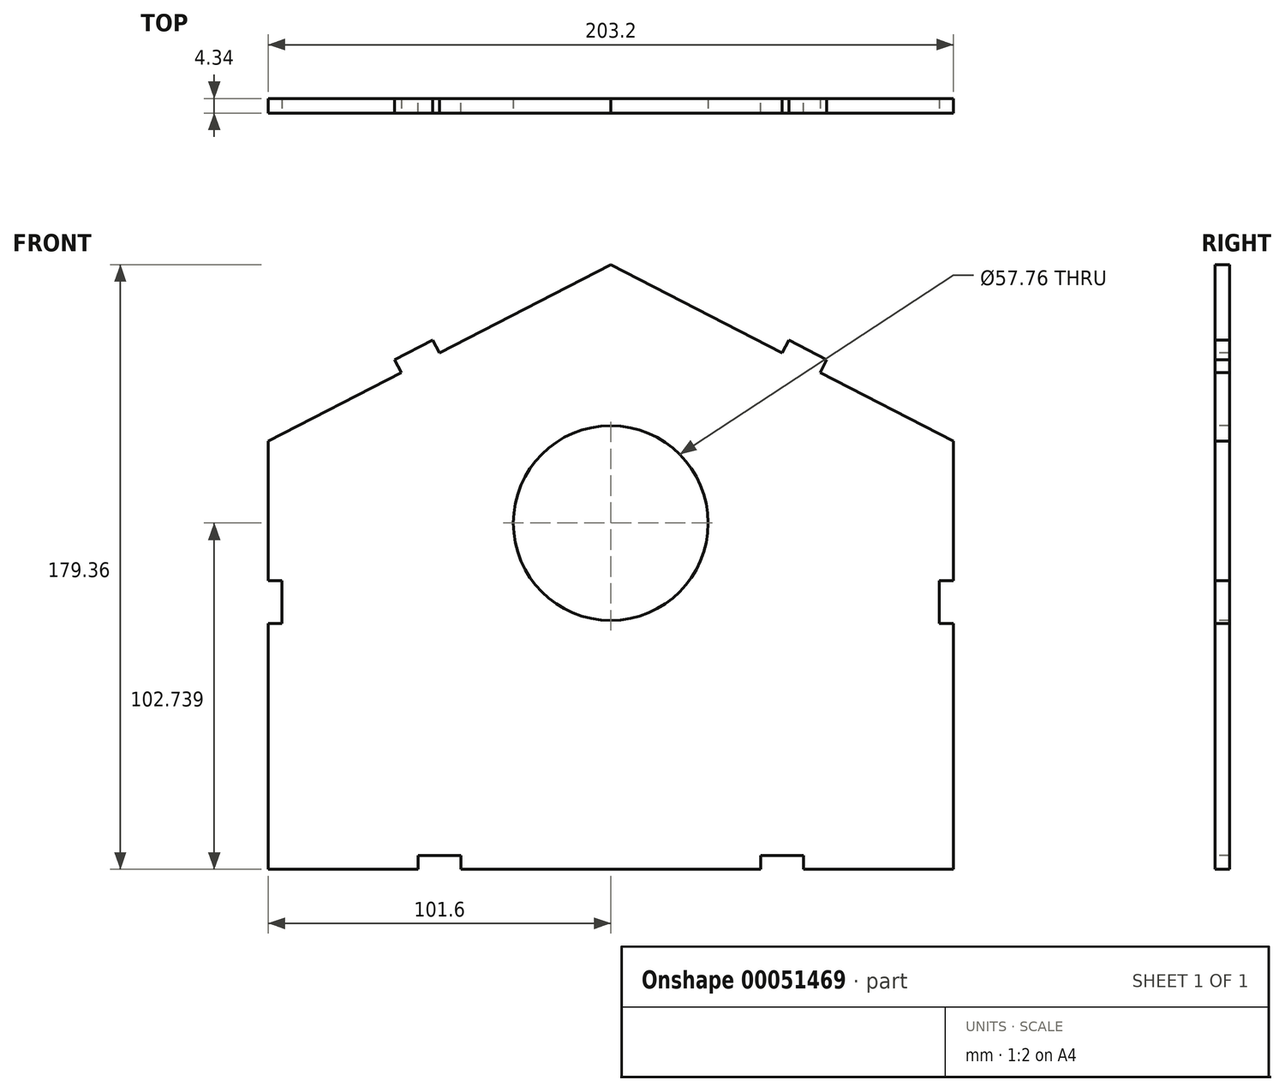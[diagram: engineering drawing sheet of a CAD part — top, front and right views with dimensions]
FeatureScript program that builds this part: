
annotation { "Feature Type Name" : "Feature", "Feature Type Description" : "" }
export const myFeature = defineFeature(function(context is Context, id is Id, definition is map)
    precondition{}
    {
        {
            var Q0;
            Q0=qCreatedBy(makeId("Front.planeOp"),FACE);
            var sketch = newSketch(context, id + "F0", { "sketchPlane" : qUnion([Q0])});
            skLineSegment(sketch, "E0", {"start": v(0, 100.27) * mm, "end": v(-101.6, 47.9) * mm});
            skLineSegment(sketch, "E1", {"start": v(0, 100.27) * mm, "end": v(101.6, 47.9) * mm});
            skLineSegment(sketch, "E2", {"start": v(-101.6, 47.9) * mm, "end": v(-101.6, -79.1) * mm});
            skLineSegment(sketch, "E3", {"start": v(-101.6, -79.1) * mm, "end": v(-57.15, -79.1) * mm});
            skLineSegment(sketch, "E4", {"start": v(101.6, -79.1) * mm, "end": v(101.6, 47.9) * mm});
            skLineSegment(sketch, "E5", {"start": v(-50.8, 74.09) * mm, "end": v(-52.79, 77.95) * mm});
            skLineSegment(sketch, "E6", {"start": v(-52.79, 77.95) * mm, "end": v(-64.08, 72.13) * mm});
            skLineSegment(sketch, "E7", {"start": v(-64.08, 72.13) * mm, "end": v(-62.09, 68.27) * mm});
            skLineSegment(sketch, "E8", {"start": v(50.8, 74.09) * mm, "end": v(52.79, 77.95) * mm});
            skLineSegment(sketch, "E9", {"start": v(52.79, 77.95) * mm, "end": v(64.08, 72.13) * mm});
            skLineSegment(sketch, "E10", {"start": v(64.08, 72.13) * mm, "end": v(62.09, 68.27) * mm});
            skPoint(sketch, "E11.MirrorCS.start.orphan", {"position": v(-50.8, -74.75) * mm});
            skPoint(sketch, "E12.start.orphan", {"position": v(-44.45, -74.75) * mm});
            skPoint(sketch, "E13.end.orphan", {"position": v(-57.15, -74.75) * mm});
            skLineSegment(sketch, "E14", {"start": v(-44.45, -79.1) * mm, "end": v(-57.15, -79.1) * mm});
            skPoint(sketch, "E15.MirrorCS.start.orphan", {"position": v(50.8, -74.75) * mm});
            skPoint(sketch, "E16.start.orphan", {"position": v(57.15, -74.75) * mm});
            skPoint(sketch, "E17.end.orphan", {"position": v(44.45, -79.1) * mm});
            skPoint(sketch, "E17.start.orphan", {"position": v(44.45, -74.75) * mm});
            skLineSegment(sketch, "E18", {"start": v(50.8, -79.1) * mm, "end": v(44.45, -79.1) * mm});
            skLineSegment(sketch, "E19.trimOffspring", {"start": v(-50.8, -74.75) * mm, "end": v(-50.8, -79.1) * mm, "construction": true});
            skLineSegment(sketch, "E20.trimOffspring", {"start": v(50.8, -74.75) * mm, "end": v(50.8, -79.1) * mm, "construction": true});
            skPoint(sketch, "E21.end.orphan", {"position": v(0, -79.1) * mm});
            skLineSegment(sketch, "E22", {"start": v(0, 100.27) * mm, "end": v(0, -79.1) * mm, "construction": true});
            skLineSegment(sketch, "E23.trimOffspring", {"start": v(-44.45, -79.1) * mm, "end": v(44.45, -79.1) * mm});
            skLineSegment(sketch, "E24.trimOffspring", {"start": v(50.8, -79.1) * mm, "end": v(101.6, -79.1) * mm});
            skLineSegment(sketch, "E25.bottom", {"start": v(-57.15, -79.1) * mm, "end": v(-44.45, -79.1) * mm});
            skLineSegment(sketch, "E25.top", {"start": v(-57.15, -74.75) * mm, "end": v(-44.45, -74.75) * mm});
            skLineSegment(sketch, "E25.left", {"start": v(-57.15, -79.1) * mm, "end": v(-57.15, -74.75) * mm});
            skLineSegment(sketch, "E25.right", {"start": v(-44.45, -79.1) * mm, "end": v(-44.45, -74.75) * mm});
            skLineSegment(sketch, "E26.bottom", {"start": v(44.45, -79.1) * mm, "end": v(57.15, -79.1) * mm});
            skLineSegment(sketch, "E26.top", {"start": v(44.45, -74.75) * mm, "end": v(57.15, -74.75) * mm});
            skLineSegment(sketch, "E26.left", {"start": v(44.45, -79.1) * mm, "end": v(44.45, -74.75) * mm});
            skLineSegment(sketch, "E26.right", {"start": v(57.15, -79.1) * mm, "end": v(57.15, -74.75) * mm});
            skSolve(sketch);
        }
        {
            var Q0;
            Q0 = qSketchRegion(id + "F0", true);
            extrude(context, id + "F1", {"entities" : qUnion([Q0]), "oppositeDirection" : true, "depth" : 4.34 * mm});
        }
        {
            var Q0;
            Q0=qCreatedBy(makeId("Front.planeOp"),FACE);
            var sketch = newSketch(context, id + "F2", { "sketchPlane" : qUnion([Q0])});
            skLineSegment(sketch, "E27.bottom", {"start": v(-101.83, 6.57) * mm, "end": v(-97.49, 6.57) * mm});
            skLineSegment(sketch, "E27.top", {"start": v(-101.83, -6.13) * mm, "end": v(-97.49, -6.13) * mm});
            skLineSegment(sketch, "E27.left", {"start": v(-101.83, 6.57) * mm, "end": v(-101.83, -6.13) * mm});
            skLineSegment(sketch, "E27.right", {"start": v(-97.49, 6.57) * mm, "end": v(-97.49, -6.13) * mm});
            skLineSegment(sketch, "E28.MirrorCS", {"start": v(101.83, 6.57) * mm, "end": v(101.83, -6.13) * mm});
            skLineSegment(sketch, "E29.MirrorCS", {"start": v(101.83, 6.57) * mm, "end": v(97.49, 6.57) * mm});
            skLineSegment(sketch, "E30.MirrorCS", {"start": v(97.49, 6.57) * mm, "end": v(97.49, -6.13) * mm});
            skLineSegment(sketch, "E31.MirrorCS", {"start": v(101.83, -6.13) * mm, "end": v(97.49, -6.13) * mm});
            skSolve(sketch);
        }
        {
            var Q0;
            Q0 = qSketchRegion(id + "F2", true);
            extrude(context, id + "F3", {"entities" : qUnion([Q0]), "operationType" : NewBodyOperationType.REMOVE, "endBound" : BoundingType.THROUGH_ALL, "oppositeDirection" : true, "depth" : 25.4 * mm});
        }
        {
            var Q0;
            Q0=qCreatedBy(makeId("Front.planeOp"),FACE);
            var sketch = newSketch(context, id + "F4", { "sketchPlane" : qUnion([Q0])});
            skLineSegment(sketch, "E32", {"start": v(0, 100.75) * mm, "end": v(0, -81.7) * mm, "construction": true});
            skCircle(sketch, "E33", {"center": v(0, 23.65) * mm, "radius": 28.88 * mm});
            skSolve(sketch);
        }
        {
            var Q0;
            Q0 = qSketchRegion(id + "F4", true);
            extrude(context, id + "F5", {"entities" : qUnion([Q0]), "operationType" : NewBodyOperationType.REMOVE, "endBound" : BoundingType.THROUGH_ALL, "oppositeDirection" : true, "depth" : 25.4 * mm});
        }
        {
            var Q0;
            Q0=qCreatedBy(makeId("Front.planeOp"),FACE);
            var sketch = newSketch(context, id + "F6", { "sketchPlane" : qUnion([Q0])});
            skLineSegment(sketch, "E34", {"start": v(0, 100.24) * mm, "end": v(0, -79.76) * mm, "construction": true});
            skLineSegment(sketch, "E35.0", {"start": v(-50.8, 100.24) * mm, "end": v(-50.8, -79.32) * mm, "construction": true});
            skLineSegment(sketch, "E36.0", {"start": v(50.8, 100.24) * mm, "end": v(50.8, -79.76) * mm, "construction": true});
            skLineSegment(sketch, "E37", {"start": v(-50.8, -79.32) * mm, "end": v(-57.15, -79.32) * mm});
            skLineSegment(sketch, "E38", {"start": v(-57.15, -79.32) * mm, "end": v(-57.15, -74.97) * mm});
            skLineSegment(sketch, "E39", {"start": v(-57.15, -74.97) * mm, "end": v(-50.8, -74.97) * mm});
            skLineSegment(sketch, "E40.MirrorCS", {"start": v(-44.45, -74.97) * mm, "end": v(-50.8, -74.97) * mm});
            skLineSegment(sketch, "E41.MirrorCS", {"start": v(-44.45, -79.32) * mm, "end": v(-44.45, -74.97) * mm});
            skLineSegment(sketch, "E42.MirrorCS", {"start": v(-50.8, -79.32) * mm, "end": v(-44.45, -79.32) * mm});
            skLineSegment(sketch, "E43.MirrorCS", {"start": v(57.15, -74.97) * mm, "end": v(50.8, -74.97) * mm});
            skLineSegment(sketch, "E44.MirrorCS", {"start": v(44.45, -74.97) * mm, "end": v(50.8, -74.97) * mm});
            skLineSegment(sketch, "E45.MirrorCS", {"start": v(44.45, -79.32) * mm, "end": v(44.45, -74.97) * mm});
            skLineSegment(sketch, "E46.MirrorCS", {"start": v(50.8, -79.32) * mm, "end": v(44.45, -79.32) * mm});
            skLineSegment(sketch, "E47.MirrorCS", {"start": v(50.8, -79.32) * mm, "end": v(57.15, -79.32) * mm});
            skLineSegment(sketch, "E48.MirrorCS", {"start": v(57.15, -79.32) * mm, "end": v(57.15, -74.97) * mm});
            skSolve(sketch);
        }
        {
            var Q0;
            Q0 = qSketchRegion(id + "F6", true);
            extrude(context, id + "F7", {"entities" : qUnion([Q0]), "operationType" : NewBodyOperationType.REMOVE, "endBound" : BoundingType.THROUGH_ALL, "oppositeDirection" : true, "depth" : 25.4 * mm});
        }
    });
